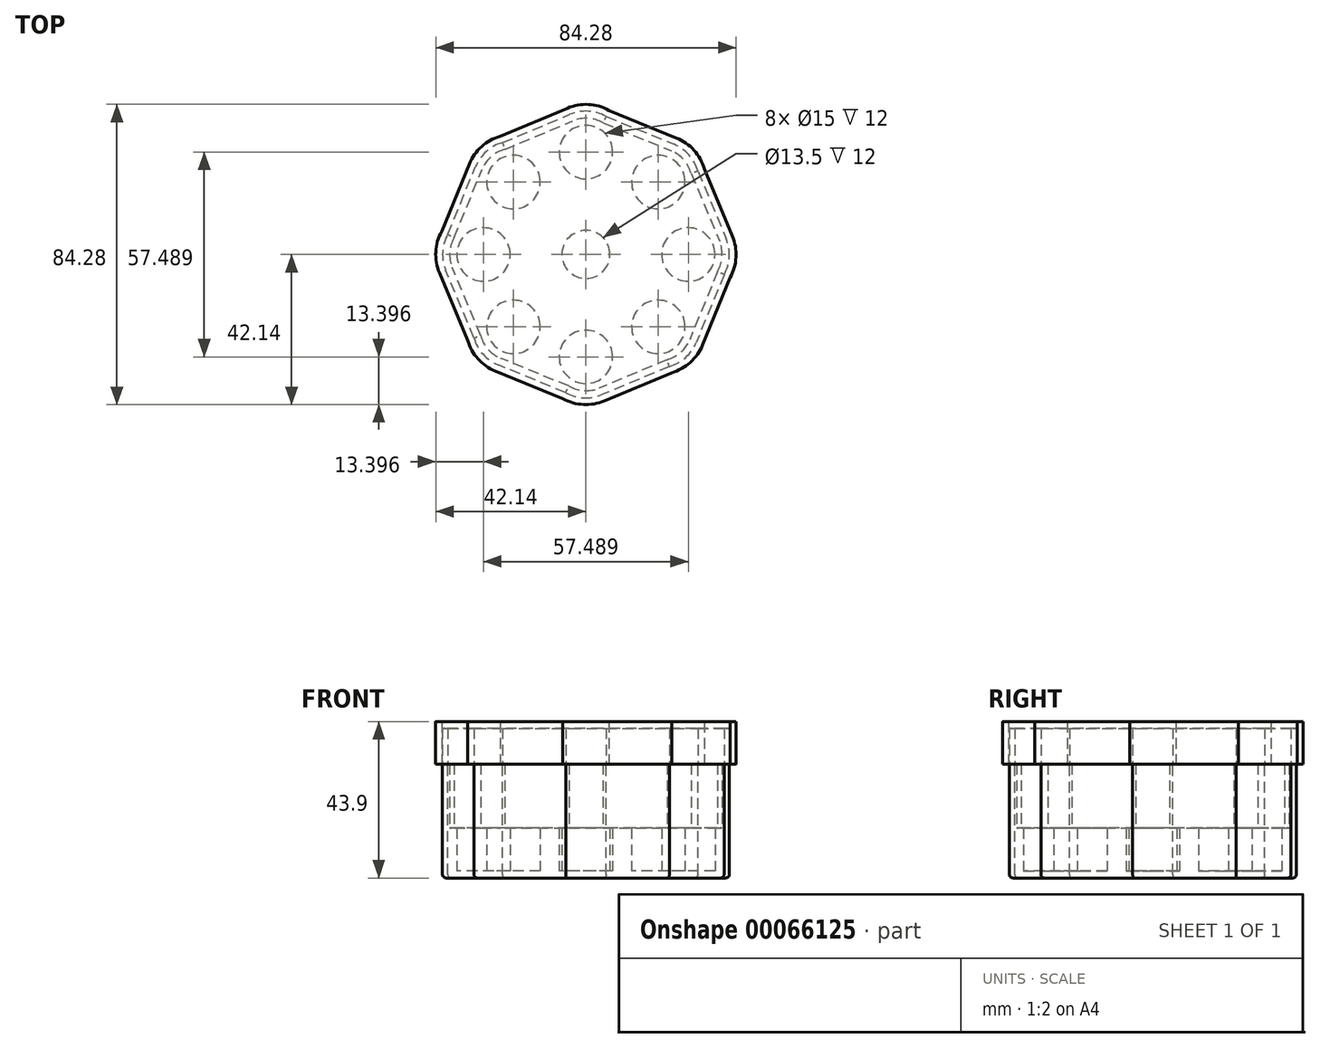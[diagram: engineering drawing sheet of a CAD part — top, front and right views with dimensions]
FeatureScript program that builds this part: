
annotation { "Feature Type Name" : "Feature", "Feature Type Description" : "" }
export const myFeature = defineFeature(function(context is Context, id is Id, definition is map)
    precondition{}
    {
        {
            var Q0;
            Q0=qCreatedBy(makeId("Top.planeOp"),FACE);
            var sketch = newSketch(context, id + "F0", { "sketchPlane" : qUnion([Q0])});
            skCircle(sketch, "E0", {"center": v(0, 28.74) * mm, "radius": 7.5 * mm});
            skCircle(sketch, "E1.1.0", {"center": v(-20.33, 20.33) * mm, "radius": 7.5 * mm});
            skCircle(sketch, "E1.2.0", {"center": v(-28.74, 0) * mm, "radius": 7.5 * mm});
            skCircle(sketch, "E1.3.0", {"center": v(-20.33, -20.33) * mm, "radius": 7.5 * mm});
            skCircle(sketch, "E1.4.0", {"center": v(0, -28.74) * mm, "radius": 7.5 * mm});
            skCircle(sketch, "E1.5.0", {"center": v(20.33, -20.33) * mm, "radius": 7.5 * mm});
            skCircle(sketch, "E1.6.0", {"center": v(28.74, 0) * mm, "radius": 7.5 * mm});
            skCircle(sketch, "E1.7.0", {"center": v(20.33, 20.33) * mm, "radius": 7.5 * mm});
            skPoint(sketch, "E1.center", {"position": v(0, 0) * mm});
            skCircle(sketch, "E2", {"center": v(0, 0) * mm, "radius": 6.75 * mm});
            skCircle(sketch, "E3", {"center": v(0, 28.74) * mm, "radius": 9.5 * mm});
            skCircle(sketch, "E4.1.0", {"center": v(-20.33, 20.33) * mm, "radius": 9.5 * mm});
            skCircle(sketch, "E4.2.0", {"center": v(-28.74, 0) * mm, "radius": 9.5 * mm});
            skCircle(sketch, "E4.3.0", {"center": v(-20.33, -20.33) * mm, "radius": 9.5 * mm});
            skCircle(sketch, "E4.4.0", {"center": v(0, -28.74) * mm, "radius": 9.5 * mm});
            skCircle(sketch, "E4.5.0", {"center": v(20.33, -20.33) * mm, "radius": 9.5 * mm});
            skCircle(sketch, "E4.6.0", {"center": v(28.74, 0) * mm, "radius": 9.5 * mm});
            skCircle(sketch, "E4.7.0", {"center": v(20.33, 20.33) * mm, "radius": 9.5 * mm});
            skLineSegment(sketch, "E5", {"start": v(2.36, 37.95) * mm, "end": v(23.93, 29.12) * mm});
            skLineSegment(sketch, "E6.1.0", {"start": v(-25.16, 28.5) * mm, "end": v(-3.67, 37.5) * mm});
            skLineSegment(sketch, "E6.2.0", {"start": v(-37.95, 2.36) * mm, "end": v(-29.12, 23.93) * mm});
            skLineSegment(sketch, "E6.3.0", {"start": v(-28.5, -25.16) * mm, "end": v(-37.5, -3.67) * mm});
            skLineSegment(sketch, "E6.4.0", {"start": v(-2.36, -37.95) * mm, "end": v(-23.93, -29.12) * mm});
            skLineSegment(sketch, "E6.5.0", {"start": v(25.16, -28.5) * mm, "end": v(3.67, -37.5) * mm});
            skLineSegment(sketch, "E6.6.0", {"start": v(37.95, -2.36) * mm, "end": v(29.12, -23.93) * mm});
            skLineSegment(sketch, "E6.7.0", {"start": v(28.5, 25.16) * mm, "end": v(37.5, 3.67) * mm});
            skSolve(sketch);
        }
        {
            var Q0;
            Q0 = qSketchRegion(id + "F0", true);
            extrude(context, id + "F1", {"entities" : qUnion([Q0]), "depth" : 12 * mm});
        }
        {
            var Q0;
            Q0=makeQuery(id+"F1.opExtrude","CAP_FACE",FACE,{"disambiguationData":[OSD([sQuery(id+"F0.wireOp",EDGE,"E0"),sQuery(id+"F0.wireOp",EDGE,"E1.1.0"),sQuery(id+"F0.wireOp",EDGE,"E1.2.0"),sQuery(id+"F0.wireOp",EDGE,"E1.3.0"),sQuery(id+"F0.wireOp",EDGE,"E1.4.0"),sQuery(id+"F0.wireOp",EDGE,"E1.5.0"),sQuery(id+"F0.wireOp",EDGE,"E1.6.0"),sQuery(id+"F0.wireOp",EDGE,"E1.7.0"),sQuery(id+"F0.wireOp",EDGE,"E2"),sQuery(id+"F0.wireOp",EDGE,"E3"),sQuery(id+"F0.wireOp",EDGE,"E4.1.0"),sQuery(id+"F0.wireOp",EDGE,"E4.2.0"),sQuery(id+"F0.wireOp",EDGE,"E4.3.0"),sQuery(id+"F0.wireOp",EDGE,"E4.4.0"),sQuery(id+"F0.wireOp",EDGE,"E4.5.0"),sQuery(id+"F0.wireOp",EDGE,"E4.6.0"),sQuery(id+"F0.wireOp",EDGE,"E4.7.0"),sQuery(id+"F0.wireOp",EDGE,"E5"),sQuery(id+"F0.wireOp",EDGE,"E6.1.0"),sQuery(id+"F0.wireOp",EDGE,"E6.2.0"),sQuery(id+"F0.wireOp",EDGE,"E6.3.0"),sQuery(id+"F0.wireOp",EDGE,"E6.4.0"),sQuery(id+"F0.wireOp",EDGE,"E6.5.0"),sQuery(id+"F0.wireOp",EDGE,"E6.6.0"),sQuery(id+"F0.wireOp",EDGE,"E6.7.0")])],"isStart":true});
            var sketch = newSketch(context, id + "F2", { "sketchPlane" : qUnion([Q0])});
            skLineSegment(sketch, "E7.0", {"start": v(-4.77, 36.96) * mm, "end": v(-23.93, 29.12) * mm});
            skArc(sketch, "E8.0", {"start": v(-4.77, 36.96) * mm, "mid": v(-0.61, 38.22) * mm, "end": v(3.67, 37.5) * mm});
            skLineSegment(sketch, "E9.0", {"start": v(22.76, 29.5) * mm, "end": v(3.67, 37.5) * mm});
            skArc(sketch, "E10.0", {"start": v(22.76, 29.5) * mm, "mid": v(26.6, 27.46) * mm, "end": v(29.12, 23.93) * mm});
            skLineSegment(sketch, "E11.0", {"start": v(36.96, 4.77) * mm, "end": v(29.12, 23.93) * mm});
            skArc(sketch, "E12.0", {"start": v(36.96, 4.77) * mm, "mid": v(38.22, 0.61) * mm, "end": v(37.5, -3.67) * mm});
            skLineSegment(sketch, "E13.0", {"start": v(29.5, -22.76) * mm, "end": v(37.5, -3.67) * mm});
            skArc(sketch, "E14.0", {"start": v(29.5, -22.76) * mm, "mid": v(27.46, -26.6) * mm, "end": v(23.93, -29.12) * mm});
            skLineSegment(sketch, "E15.0", {"start": v(4.77, -36.96) * mm, "end": v(23.93, -29.12) * mm});
            skArc(sketch, "E16.0", {"start": v(4.77, -36.96) * mm, "mid": v(0.61, -38.22) * mm, "end": v(-3.67, -37.5) * mm});
            skLineSegment(sketch, "E17.0", {"start": v(-22.76, -29.5) * mm, "end": v(-3.67, -37.5) * mm});
            skArc(sketch, "E18.0", {"start": v(-22.76, -29.5) * mm, "mid": v(-26.6, -27.46) * mm, "end": v(-29.12, -23.93) * mm});
            skLineSegment(sketch, "E19.0", {"start": v(-36.96, -4.77) * mm, "end": v(-29.12, -23.93) * mm});
            skArc(sketch, "E20.0", {"start": v(-36.96, -4.77) * mm, "mid": v(-38.22, -0.61) * mm, "end": v(-37.5, 3.67) * mm});
            skLineSegment(sketch, "E21.0", {"start": v(-29.5, 22.76) * mm, "end": v(-37.5, 3.67) * mm});
            skArc(sketch, "E22.0", {"start": v(-29.5, 22.76) * mm, "mid": v(-27.46, 26.6) * mm, "end": v(-23.93, 29.12) * mm});
            skArc(sketch, "E23.0", {"start": v(-38.76, -5.65) * mm, "mid": v(-40.22, -0.67) * mm, "end": v(-39.35, 4.44) * mm});
            skLineSegment(sketch, "E23.1", {"start": v(-31.4, 23.41) * mm, "end": v(-39.35, 4.44) * mm});
            skArc(sketch, "E23.2", {"start": v(-31.4, 23.41) * mm, "mid": v(-28.92, 27.97) * mm, "end": v(-24.68, 30.97) * mm});
            skLineSegment(sketch, "E23.3", {"start": v(-5.65, 38.76) * mm, "end": v(-24.68, 30.97) * mm});
            skArc(sketch, "E23.4", {"start": v(-5.65, 38.76) * mm, "mid": v(-0.67, 40.22) * mm, "end": v(4.44, 39.35) * mm});
            skLineSegment(sketch, "E23.5", {"start": v(5.65, -38.76) * mm, "end": v(24.68, -30.97) * mm});
            skArc(sketch, "E23.6", {"start": v(5.65, -38.76) * mm, "mid": v(0.67, -40.22) * mm, "end": v(-4.44, -39.35) * mm});
            skLineSegment(sketch, "E23.7", {"start": v(-23.41, -31.4) * mm, "end": v(-4.44, -39.35) * mm});
            skArc(sketch, "E23.8", {"start": v(-23.41, -31.4) * mm, "mid": v(-27.97, -28.92) * mm, "end": v(-30.97, -24.68) * mm});
            skArc(sketch, "E23.9", {"start": v(31.4, -23.41) * mm, "mid": v(28.92, -27.97) * mm, "end": v(24.68, -30.97) * mm});
            skLineSegment(sketch, "E23.10", {"start": v(31.4, -23.41) * mm, "end": v(39.35, -4.44) * mm});
            skArc(sketch, "E23.11", {"start": v(38.76, 5.65) * mm, "mid": v(40.22, 0.67) * mm, "end": v(39.35, -4.44) * mm});
            skLineSegment(sketch, "E23.12", {"start": v(38.76, 5.65) * mm, "end": v(30.97, 24.68) * mm});
            skArc(sketch, "E23.13", {"start": v(23.41, 31.4) * mm, "mid": v(27.97, 28.92) * mm, "end": v(30.97, 24.68) * mm});
            skLineSegment(sketch, "E23.14", {"start": v(-38.76, -5.65) * mm, "end": v(-30.97, -24.68) * mm});
            skLineSegment(sketch, "E23.15", {"start": v(23.41, 31.4) * mm, "end": v(4.44, 39.35) * mm});
            skSolve(sketch);
        }
        {
            var Q0;
            Q0=makeQuery(id+"F2.imprint","IMPRINT",FACE,{"disambiguationData":[TD([[makeQuery(id+"F2.imprint","IMPRINT",EDGE,{"derivedFrom":sQuery(id+"F2.wireOp",EDGE,"E7.0")}),-1.0]])]});
            var Q1;
            Q1=makeQuery(id+"F2.imprint","IMPRINT",FACE,{"disambiguationData":[TD([[makeQuery(id+"F2.imprint","IMPRINT",EDGE,{"derivedFrom":sQuery(id+"F2.wireOp",EDGE,"E7.0")}),1.0]])]});
            var Q2;
            Q2=makeQuery(id+"F2.imprint","IMPRINT",FACE,{"disambiguationData":[TD([[makeQuery(id+"F2.imprint","IMPRINT",EDGE,{"derivedFrom":makeQuery(id+"F1.opExtrude","CAP_EDGE",EDGE,{"disambiguationData":[OSD([sQuery(id+"F0.wireOp",EDGE,"E1.2.0")])],"isStart":true})}),-1.0]])]});
            var Q3;
            Q3=makeQuery(id+"F2.imprint","IMPRINT",FACE,{"disambiguationData":[TD([[makeQuery(id+"F2.imprint","IMPRINT",EDGE,{"derivedFrom":makeQuery(id+"F1.opExtrude","CAP_EDGE",EDGE,{"disambiguationData":[OSD([sQuery(id+"F0.wireOp",EDGE,"E1.3.0")])],"isStart":true})}),-1.0]])]});
            var Q4;
            Q4=makeQuery(id+"F2.imprint","IMPRINT",FACE,{"disambiguationData":[TD([[makeQuery(id+"F2.imprint","IMPRINT",EDGE,{"derivedFrom":makeQuery(id+"F1.opExtrude","CAP_EDGE",EDGE,{"disambiguationData":[OSD([sQuery(id+"F0.wireOp",EDGE,"E2")])],"isStart":true})}),-1.0]])]});
            var Q5;
            Q5=makeQuery(id+"F2.imprint","IMPRINT",FACE,{"disambiguationData":[TD([[makeQuery(id+"F2.imprint","IMPRINT",EDGE,{"derivedFrom":makeQuery(id+"F1.opExtrude","CAP_EDGE",EDGE,{"disambiguationData":[OSD([sQuery(id+"F0.wireOp",EDGE,"E1.6.0")])],"isStart":true})}),-1.0]])]});
            var Q6;
            Q6=makeQuery(id+"F2.imprint","IMPRINT",FACE,{"disambiguationData":[TD([[makeQuery(id+"F2.imprint","IMPRINT",EDGE,{"derivedFrom":makeQuery(id+"F1.opExtrude","CAP_EDGE",EDGE,{"disambiguationData":[OSD([sQuery(id+"F0.wireOp",EDGE,"E1.5.0")])],"isStart":true})}),-1.0]])]});
            var Q7;
            Q7=makeQuery(id+"F2.imprint","IMPRINT",FACE,{"disambiguationData":[TD([[makeQuery(id+"F2.imprint","IMPRINT",EDGE,{"derivedFrom":makeQuery(id+"F1.opExtrude","CAP_EDGE",EDGE,{"disambiguationData":[OSD([sQuery(id+"F0.wireOp",EDGE,"E1.4.0")])],"isStart":true})}),-1.0]])]});
            var Q8;
            Q8=makeQuery(id+"F2.imprint","IMPRINT",FACE,{"disambiguationData":[TD([[makeQuery(id+"F2.imprint","IMPRINT",EDGE,{"derivedFrom":makeQuery(id+"F1.opExtrude","CAP_EDGE",EDGE,{"disambiguationData":[OSD([sQuery(id+"F0.wireOp",EDGE,"E1.7.0")])],"isStart":true})}),-1.0]])]});
            var Q9;
            Q9=makeQuery(id+"F2.imprint","IMPRINT",FACE,{"disambiguationData":[TD([[makeQuery(id+"F2.imprint","IMPRINT",EDGE,{"derivedFrom":makeQuery(id+"F1.opExtrude","CAP_EDGE",EDGE,{"disambiguationData":[OSD([sQuery(id+"F0.wireOp",EDGE,"E0")])],"isStart":true})}),-1.0]])]});
            var Q10;
            Q10=makeQuery(id+"F2.imprint","IMPRINT",FACE,{"disambiguationData":[TD([[makeQuery(id+"F2.imprint","IMPRINT",EDGE,{"derivedFrom":makeQuery(id+"F1.opExtrude","CAP_EDGE",EDGE,{"disambiguationData":[OSD([sQuery(id+"F0.wireOp",EDGE,"E1.1.0")])],"isStart":true})}),-1.0]])]});
            extrude(context, id + "F3", {"entities" : qUnion([Q0, Q1, Q2, Q3, Q4, Q5, Q6, Q7, Q8, Q9, Q10]), "operationType" : NewBodyOperationType.ADD, "depth" : 2 * mm});
        }
        {
            var Q0;
            Q0=makeQuery(id+"F2.imprint","IMPRINT",FACE,{"disambiguationData":[TD([[makeQuery(id+"F2.imprint","IMPRINT",EDGE,{"derivedFrom":sQuery(id+"F2.wireOp",EDGE,"E7.0")}),-1.0]])]});
            extrude(context, id + "F4", {"entities" : qUnion([Q0]), "operationType" : NewBodyOperationType.ADD, "oppositeDirection" : true, "depth" : 30 * mm});
        }
        {
            var Q0;
            Q0=makeQuery(id+"F3.opExtrude","CAP_EDGE",EDGE,{"disambiguationData":[OSD([sQuery(id+"F2.wireOp",EDGE,"E23.14")])],"isStart":false});
            var Q1;
            Q1=makeQuery(id+"F3.opExtrude","CAP_EDGE",EDGE,{"disambiguationData":[OSD([sQuery(id+"F2.wireOp",EDGE,"E23.8")])],"isStart":false});
            var Q2;
            Q2=makeQuery(id+"F3.opExtrude","CAP_EDGE",EDGE,{"disambiguationData":[OSD([sQuery(id+"F2.wireOp",EDGE,"E23.7")])],"isStart":false});
            var Q3;
            Q3=makeQuery(id+"F3.opExtrude","CAP_EDGE",EDGE,{"disambiguationData":[OSD([sQuery(id+"F2.wireOp",EDGE,"E23.0")])],"isStart":false});
            var Q4;
            Q4=makeQuery(id+"F3.opExtrude","CAP_EDGE",EDGE,{"disambiguationData":[OSD([sQuery(id+"F2.wireOp",EDGE,"E23.1")])],"isStart":false});
            var Q5;
            Q5=makeQuery(id+"F3.opExtrude","CAP_EDGE",EDGE,{"disambiguationData":[OSD([sQuery(id+"F2.wireOp",EDGE,"E23.2")])],"isStart":false});
            var Q6;
            Q6=makeQuery(id+"F3.opExtrude","CAP_EDGE",EDGE,{"disambiguationData":[OSD([sQuery(id+"F2.wireOp",EDGE,"E23.3")])],"isStart":false});
            var Q7;
            Q7=makeQuery(id+"F3.opExtrude","CAP_EDGE",EDGE,{"disambiguationData":[OSD([sQuery(id+"F2.wireOp",EDGE,"E23.15")])],"isStart":false});
            var Q8;
            Q8=makeQuery(id+"F3.opExtrude","CAP_EDGE",EDGE,{"disambiguationData":[OSD([sQuery(id+"F2.wireOp",EDGE,"E23.4")])],"isStart":false});
            var Q9;
            Q9=makeQuery(id+"F3.opExtrude","CAP_EDGE",EDGE,{"disambiguationData":[OSD([sQuery(id+"F2.wireOp",EDGE,"E23.13")])],"isStart":false});
            var Q10;
            Q10=makeQuery(id+"F3.opExtrude","CAP_EDGE",EDGE,{"disambiguationData":[OSD([sQuery(id+"F2.wireOp",EDGE,"E23.12")])],"isStart":false});
            var Q11;
            Q11=makeQuery(id+"F3.opExtrude","CAP_EDGE",EDGE,{"disambiguationData":[OSD([sQuery(id+"F2.wireOp",EDGE,"E23.11")])],"isStart":false});
            var Q12;
            Q12=makeQuery(id+"F3.opExtrude","CAP_EDGE",EDGE,{"disambiguationData":[OSD([sQuery(id+"F2.wireOp",EDGE,"E23.10")])],"isStart":false});
            var Q13;
            Q13=makeQuery(id+"F3.opExtrude","CAP_EDGE",EDGE,{"disambiguationData":[OSD([sQuery(id+"F2.wireOp",EDGE,"E23.9")])],"isStart":false});
            var Q14;
            Q14=makeQuery(id+"F3.opExtrude","CAP_EDGE",EDGE,{"disambiguationData":[OSD([sQuery(id+"F2.wireOp",EDGE,"E23.5")])],"isStart":false});
            var Q15;
            Q15=makeQuery(id+"F3.opExtrude","CAP_EDGE",EDGE,{"disambiguationData":[OSD([sQuery(id+"F2.wireOp",EDGE,"E23.6")])],"isStart":false});
            fillet(context, id + "F5", {"entities" : qUnion([Q0, Q1, Q2, Q3, Q4, Q5, Q6, Q7, Q8, Q9, Q10, Q11, Q12, Q13, Q14, Q15]), "radius" : 1 * mm, "tangentPropagation" : true, "allowEdgeOverflow" : false});
        }
        {
            var Q0;
            Q0=makeQuery(id+"F4.opExtrude","CAP_FACE",FACE,{"disambiguationData":[OSD([sQuery(id+"F2.wireOp",EDGE,"E7.0"),sQuery(id+"F2.wireOp",EDGE,"E8.0"),sQuery(id+"F2.wireOp",EDGE,"E9.0"),sQuery(id+"F2.wireOp",EDGE,"E10.0"),sQuery(id+"F2.wireOp",EDGE,"E11.0"),sQuery(id+"F2.wireOp",EDGE,"E12.0"),sQuery(id+"F2.wireOp",EDGE,"E13.0"),sQuery(id+"F2.wireOp",EDGE,"E14.0"),sQuery(id+"F2.wireOp",EDGE,"E15.0"),sQuery(id+"F2.wireOp",EDGE,"E16.0"),sQuery(id+"F2.wireOp",EDGE,"E17.0"),sQuery(id+"F2.wireOp",EDGE,"E18.0"),sQuery(id+"F2.wireOp",EDGE,"E19.0"),sQuery(id+"F2.wireOp",EDGE,"E20.0"),sQuery(id+"F2.wireOp",EDGE,"E21.0"),sQuery(id+"F2.wireOp",EDGE,"E22.0"),sQuery(id+"F2.wireOp",EDGE,"E23.0"),sQuery(id+"F2.wireOp",EDGE,"E23.1"),sQuery(id+"F2.wireOp",EDGE,"E23.2"),sQuery(id+"F2.wireOp",EDGE,"E23.3"),sQuery(id+"F2.wireOp",EDGE,"E23.4"),sQuery(id+"F2.wireOp",EDGE,"E23.5"),sQuery(id+"F2.wireOp",EDGE,"E23.6"),sQuery(id+"F2.wireOp",EDGE,"E23.7"),sQuery(id+"F2.wireOp",EDGE,"E23.8"),sQuery(id+"F2.wireOp",EDGE,"E23.9"),sQuery(id+"F2.wireOp",EDGE,"E23.10"),sQuery(id+"F2.wireOp",EDGE,"E23.11"),sQuery(id+"F2.wireOp",EDGE,"E23.12"),sQuery(id+"F2.wireOp",EDGE,"E23.13"),sQuery(id+"F2.wireOp",EDGE,"E23.14"),sQuery(id+"F2.wireOp",EDGE,"E23.15")])],"isStart":false});
            var sketch = newSketch(context, id + "F6", { "sketchPlane" : qUnion([Q0])});
            skArc(sketch, "E24.0", {"start": v(-23.41, 31.4) * mm, "mid": v(-27.97, 28.92) * mm, "end": v(-30.97, 24.68) * mm});
            skLineSegment(sketch, "E25.0", {"start": v(-38.76, 5.65) * mm, "end": v(-30.97, 24.68) * mm});
            skArc(sketch, "E26.0", {"start": v(-38.76, 5.65) * mm, "mid": v(-40.22, 0.67) * mm, "end": v(-39.35, -4.44) * mm});
            skLineSegment(sketch, "E27.0", {"start": v(-31.4, -23.41) * mm, "end": v(-39.35, -4.44) * mm});
            skArc(sketch, "E28.0", {"start": v(-31.4, -23.41) * mm, "mid": v(-28.92, -27.97) * mm, "end": v(-24.68, -30.97) * mm});
            skLineSegment(sketch, "E29.0", {"start": v(-5.65, -38.76) * mm, "end": v(-24.68, -30.97) * mm});
            skArc(sketch, "E30.0", {"start": v(-5.65, -38.76) * mm, "mid": v(-0.67, -40.22) * mm, "end": v(4.44, -39.35) * mm});
            skLineSegment(sketch, "E31.0", {"start": v(23.41, -31.4) * mm, "end": v(4.44, -39.35) * mm});
            skArc(sketch, "E32.0", {"start": v(23.41, -31.4) * mm, "mid": v(27.97, -28.92) * mm, "end": v(30.97, -24.68) * mm});
            skLineSegment(sketch, "E33.0", {"start": v(38.76, -5.65) * mm, "end": v(30.97, -24.68) * mm});
            skArc(sketch, "E34.0", {"start": v(38.76, -5.65) * mm, "mid": v(40.22, -0.67) * mm, "end": v(39.35, 4.44) * mm});
            skLineSegment(sketch, "E35.0", {"start": v(31.4, 23.41) * mm, "end": v(39.35, 4.44) * mm});
            skArc(sketch, "E36.0", {"start": v(31.4, 23.41) * mm, "mid": v(28.92, 27.97) * mm, "end": v(24.68, 30.97) * mm});
            skLineSegment(sketch, "E37.0", {"start": v(-23.41, 31.4) * mm, "end": v(-4.44, 39.35) * mm});
            skArc(sketch, "E38.0", {"start": v(5.65, 38.76) * mm, "mid": v(0.67, 40.22) * mm, "end": v(-4.44, 39.35) * mm});
            skLineSegment(sketch, "E39.0", {"start": v(5.65, 38.76) * mm, "end": v(24.68, 30.97) * mm});
            skSolve(sketch);
        }
        {
            var Q0;
            Q0 = qSketchRegion(id + "F6", true);
            extrude(context, id + "F7", {"entities" : qUnion([Q0]), "depth" : 10 * mm});
        }
        {
            var Q0;
            Q0=makeQuery(id+"F7.opExtrude","CAP_FACE",FACE,{"disambiguationData":[OSD([sQuery(id+"F6.wireOp",EDGE,"E24.0"),sQuery(id+"F6.wireOp",EDGE,"E25.0"),sQuery(id+"F6.wireOp",EDGE,"E26.0"),sQuery(id+"F6.wireOp",EDGE,"E27.0"),sQuery(id+"F6.wireOp",EDGE,"E28.0"),sQuery(id+"F6.wireOp",EDGE,"E29.0"),sQuery(id+"F6.wireOp",EDGE,"E30.0"),sQuery(id+"F6.wireOp",EDGE,"E31.0"),sQuery(id+"F6.wireOp",EDGE,"E32.0"),sQuery(id+"F6.wireOp",EDGE,"E33.0"),sQuery(id+"F6.wireOp",EDGE,"E34.0"),sQuery(id+"F6.wireOp",EDGE,"E35.0"),sQuery(id+"F6.wireOp",EDGE,"E36.0"),sQuery(id+"F6.wireOp",EDGE,"E37.0"),sQuery(id+"F6.wireOp",EDGE,"E38.0"),sQuery(id+"F6.wireOp",EDGE,"E39.0")])],"isStart":true});
            shell(context, id + "F8", {"entities" : qUnion([Q0]), "thickness" : 1.9 * mm, "oppositeDirection" : true});
        }
    });
